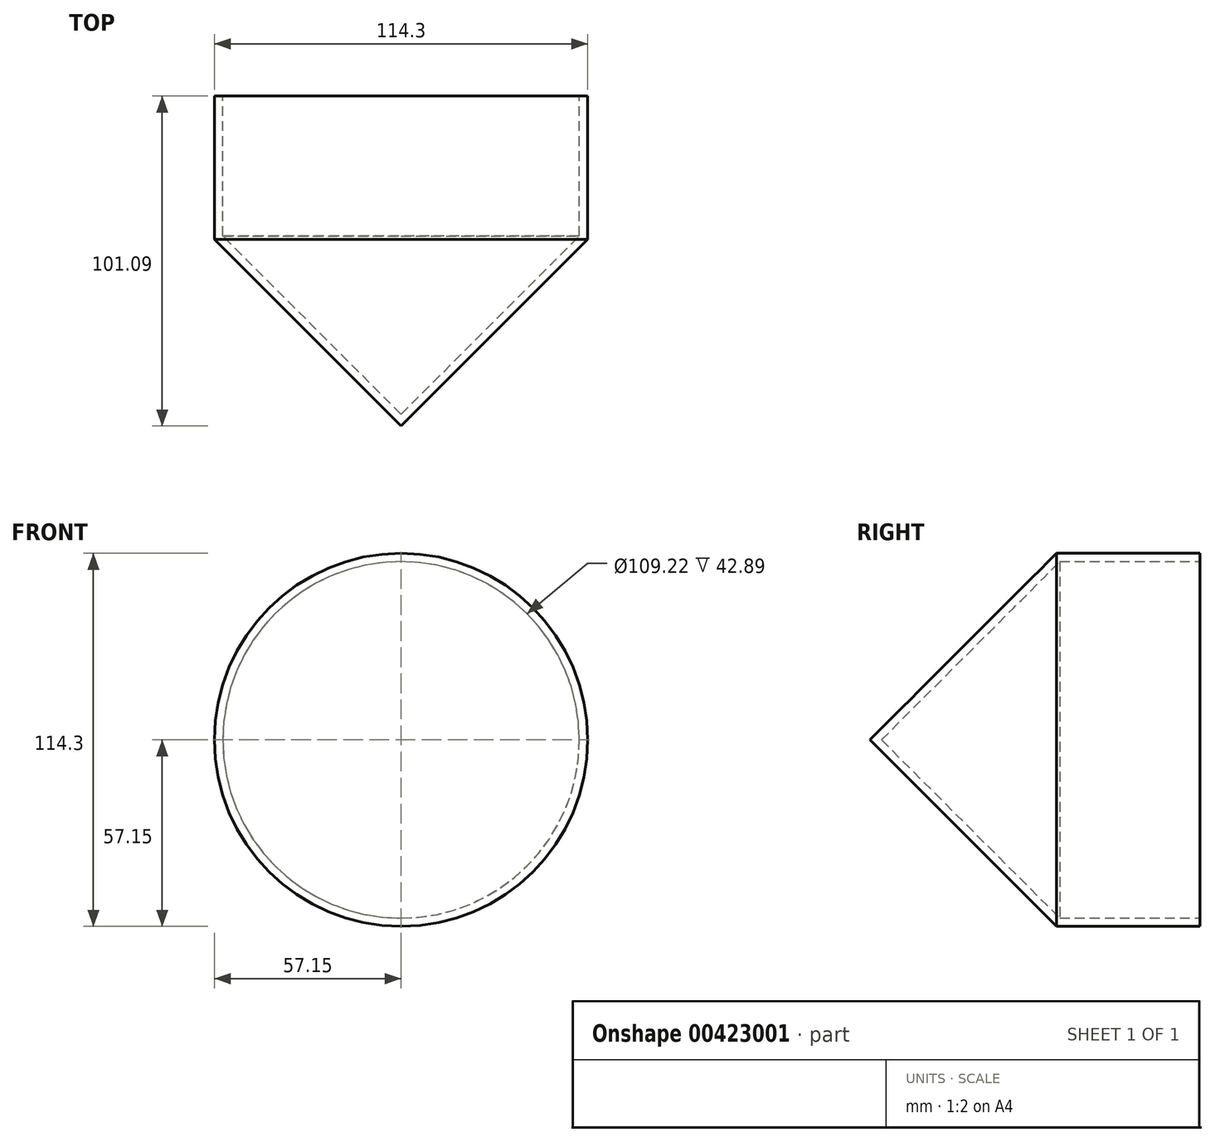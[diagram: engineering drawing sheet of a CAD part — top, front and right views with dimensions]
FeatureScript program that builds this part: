
annotation { "Feature Type Name" : "Feature", "Feature Type Description" : "" }
export const myFeature = defineFeature(function(context is Context, id is Id, definition is map)
    precondition{}
    {
        {
            var Q0;
            Q0=qCreatedBy(makeId("Front.planeOp"),FACE);
            var sketch = newSketch(context, id + "F0", { "sketchPlane" : qUnion([Q0])});
            skCircle(sketch, "E0", {"center": v(0, 0) * mm, "radius": 57.15 * mm});
            skSolve(sketch);
        }
        {
            var Q0;
            Q0=makeQuery(id+"F0.imprint","IMPRINT",FACE,{"disambiguationData":[TD([[makeQuery(id+"F0.imprint","IMPRINT",EDGE,{"derivedFrom":sQuery(id+"F0.wireOp",EDGE,"E0")}),1.0]])]});
            extrude(context, id + "F1", {"entities" : qUnion([Q0]), "depth" : 101.1 * mm});
        }
        {
            var Q0;
            Q0=makeQuery(id+"F1.opExtrude","CAP_EDGE",EDGE,{"disambiguationData":[OSD([sQuery(id+"F0.wireOp",EDGE,"E0")])],"isStart":false});
            chamfer(context, id + "F2", {"entities" : qUnion([Q0]), "width" : 57.15 * mm, "tangentPropagation" : true});
        }
        {
            var Q0;
            Q0=makeQuery(id+"F1.opExtrude","CAP_FACE",FACE,{"disambiguationData":[OSD([sQuery(id+"F0.wireOp",EDGE,"E0")])],"isStart":true});
            shell(context, id + "F3", {"entities" : qUnion([Q0]), "thickness" : 2.54 * mm});
        }
    });
